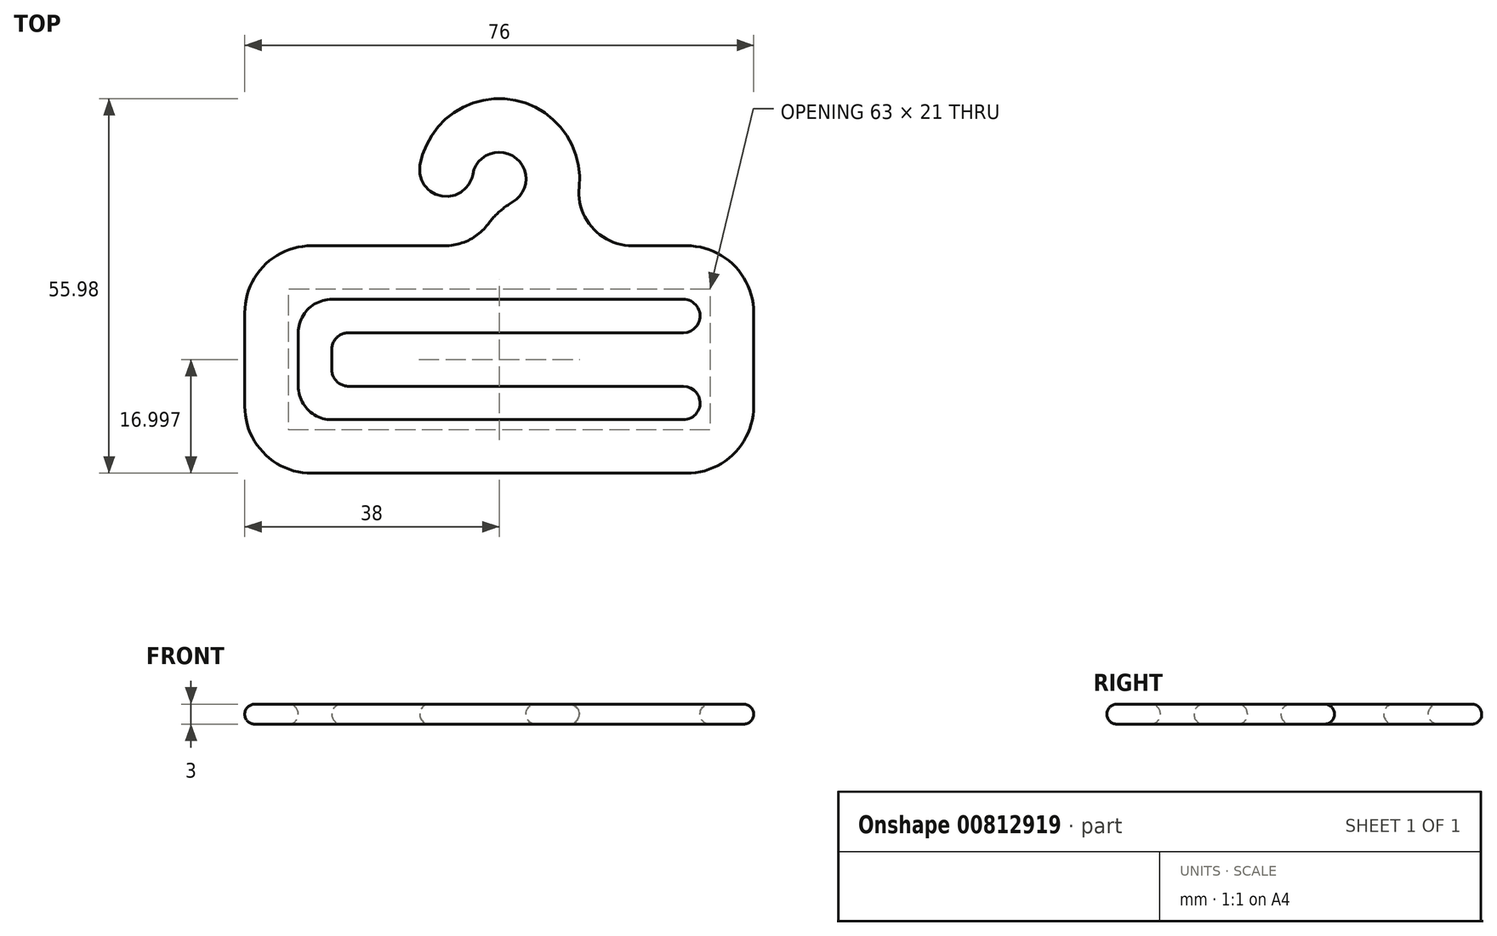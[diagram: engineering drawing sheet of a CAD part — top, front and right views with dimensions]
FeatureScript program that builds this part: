
annotation { "Feature Type Name" : "Feature", "Feature Type Description" : "" }
export const myFeature = defineFeature(function(context is Context, id is Id, definition is map)
    precondition{}
    {
        {
            var Q0;
            Q0=qCreatedBy(makeId("Top.planeOp"),FACE);
            var sketch = newSketch(context, id + "F0", { "sketchPlane" : qUnion([Q0])});
            skPoint(sketch, "E0.visualSharp", {"position": v(0, -8) * mm});
            skArc(sketch, "E0.filletArc", {"start": v(4, -6.93) * mm, "mid": v(2.3, -8.25) * mm, "end": v(1, -9.98) * mm, "construction": true});
            skArc(sketch, "E1", {"start": v(4, -6.93) * mm, "mid": v(4.58, 6.56) * mm, "end": v(-7.88, 1.37) * mm, "construction": true});
            skPoint(sketch, "E2", {"position": v(-7.88, 1.37) * mm});
            skArc(sketch, "E3.1.right", {"start": v(2, -3.46) * mm, "mid": v(0, -4.9) * mm, "end": v(-1.66, -6.73) * mm});
            skArc(sketch, "E3.2.endCap", {"start": v(-3.94, 0.68) * mm, "mid": v(-8.57, -2.57) * mm, "end": v(-11.82, 2.05) * mm});
            skArc(sketch, "E3.2.left", {"start": v(2, -3.46) * mm, "mid": v(2.29, 3.28) * mm, "end": v(-3.94, 0.68) * mm});
            skArc(sketch, "E3.2.right", {"start": v(11.94, -1.19) * mm, "mid": v(1.62, 11.89) * mm, "end": v(-11.82, 2.05) * mm});
            skLineSegment(sketch, "E4.bottom", {"start": v(28, -9.98) * mm, "end": v(19.9, -9.98) * mm});
            skLineSegment(sketch, "E4.top", {"start": v(28, -43.98) * mm, "end": v(-28, -43.98) * mm});
            skLineSegment(sketch, "E4.left", {"start": v(38, -19.98) * mm, "end": v(38, -33.98) * mm});
            skLineSegment(sketch, "E4.right", {"start": v(-38, -19.98) * mm, "end": v(-38, -33.98) * mm});
            skPoint(sketch, "E4.middle", {"position": v(0, -26.98) * mm});
            skLineSegment(sketch, "E5", {"start": v(-30, -22.98) * mm, "end": v(-30, -30.98) * mm});
            skLineSegment(sketch, "E6", {"start": v(-25, -35.98) * mm, "end": v(27.5, -35.98) * mm});
            skLineSegment(sketch, "E7", {"start": v(30, -33.48) * mm, "end": v(30, -33.48) * mm});
            skLineSegment(sketch, "E8", {"start": v(27.5, -30.98) * mm, "end": v(-22.5, -30.98) * mm});
            skLineSegment(sketch, "E9", {"start": v(-25, -28.48) * mm, "end": v(-25, -25.48) * mm});
            skLineSegment(sketch, "E10", {"start": v(-22.5, -22.98) * mm, "end": v(27.5, -22.98) * mm});
            skLineSegment(sketch, "E11", {"start": v(30, -20.48) * mm, "end": v(30, -20.48) * mm});
            skLineSegment(sketch, "E12", {"start": v(27.5, -17.98) * mm, "end": v(-25, -17.98) * mm});
            skPoint(sketch, "E13.visualSharp", {"position": v(-38, -9.98) * mm});
            skArc(sketch, "E13.filletArc", {"start": v(-28, -9.98) * mm, "mid": v(-35.07, -12.91) * mm, "end": v(-38, -19.98) * mm});
            skPoint(sketch, "E14.visualSharp", {"position": v(-30, -17.98) * mm});
            skArc(sketch, "E14.filletArc", {"start": v(-25, -17.98) * mm, "mid": v(-28.54, -19.45) * mm, "end": v(-30, -22.98) * mm});
            skArc(sketch, "E15.filletArc", {"start": v(-22.5, -22.98) * mm, "mid": v(-24.27, -23.71) * mm, "end": v(-25, -25.48) * mm});
            skPoint(sketch, "E16.visualSharp", {"position": v(-38, -43.98) * mm});
            skArc(sketch, "E16.filletArc", {"start": v(-38, -33.98) * mm, "mid": v(-35.07, -41.05) * mm, "end": v(-28, -43.98) * mm});
            skPoint(sketch, "E17.visualSharp", {"position": v(-30, -35.98) * mm});
            skArc(sketch, "E17.filletArc", {"start": v(-30, -30.98) * mm, "mid": v(-28.54, -34.52) * mm, "end": v(-25, -35.98) * mm});
            skArc(sketch, "E18.filletArc", {"start": v(-25, -28.48) * mm, "mid": v(-24.27, -30.25) * mm, "end": v(-22.5, -30.98) * mm});
            skPoint(sketch, "E19.visualSharp", {"position": v(38, -43.98) * mm});
            skArc(sketch, "E19.filletArc", {"start": v(28, -43.98) * mm, "mid": v(35.07, -41.05) * mm, "end": v(38, -33.98) * mm});
            skLineSegment(sketch, "E20", {"start": v(30, -22.98) * mm, "end": v(30, -30.98) * mm, "construction": true});
            skPoint(sketch, "E21.visualSharp", {"position": v(30, -30.98) * mm});
            skArc(sketch, "E21.filletArc", {"start": v(30, -33.48) * mm, "mid": v(29.27, -31.71) * mm, "end": v(27.5, -30.98) * mm});
            skPoint(sketch, "E22.visualSharp", {"position": v(30, -35.98) * mm});
            skArc(sketch, "E22.filletArc", {"start": v(27.5, -35.98) * mm, "mid": v(29.27, -35.25) * mm, "end": v(30, -33.48) * mm});
            skPoint(sketch, "E23.visualSharp", {"position": v(30, -17.98) * mm});
            skArc(sketch, "E23.filletArc", {"start": v(30, -20.48) * mm, "mid": v(29.27, -18.71) * mm, "end": v(27.5, -17.98) * mm});
            skPoint(sketch, "E24.visualSharp", {"position": v(30, -22.98) * mm});
            skArc(sketch, "E24.filletArc", {"start": v(27.5, -22.98) * mm, "mid": v(29.27, -22.25) * mm, "end": v(30, -20.48) * mm});
            skPoint(sketch, "E25.visualSharp", {"position": v(38, -9.98) * mm});
            skArc(sketch, "E25.filletArc", {"start": v(38, -19.98) * mm, "mid": v(35.07, -12.91) * mm, "end": v(28, -9.98) * mm});
            skArc(sketch, "E26", {"start": v(1, -9.98) * mm, "mid": v(0.25, -11.86) * mm, "end": v(0, -13.86) * mm, "construction": true});
            skLineSegment(sketch, "E27.trimOffspring", {"start": v(-8.1, -9.98) * mm, "end": v(-28, -9.98) * mm});
            skPoint(sketch, "E28.visualSharp", {"position": v(-3.36, -9.98) * mm});
            skArc(sketch, "E28.filletArc", {"start": v(-8.1, -9.98) * mm, "mid": v(-4.49, -9.12) * mm, "end": v(-1.66, -6.73) * mm});
            skPoint(sketch, "E29.visualSharp", {"position": v(6.66, -9.98) * mm});
            skArc(sketch, "E29.filletArc", {"start": v(11.94, -1.19) * mm, "mid": v(13.97, -7.35) * mm, "end": v(19.9, -9.98) * mm});
            skSolve(sketch);
        }
        {
            var Q0;
            Q0 = qSketchRegion(id + "F0", true);
            extrude(context, id + "F1", {"entities" : qUnion([Q0]), "depth" : 3 * mm, "offsetDistance" : 25 * mm});
        }
        {
            var Q0;
            Q0=makeQuery(id+"F0.imprint","IMPRINT",FACE,{"disambiguationData":[TD([[makeQuery(id+"F0.imprint","IMPRINT",EDGE,{"derivedFrom":sQuery(id+"F0.wireOp",EDGE,"E5")}),1.0]])]});
            extrude(context, id + "F2", {"entities" : qUnion([Q0]), "operationType" : NewBodyOperationType.REMOVE, "oppositeDirection" : true, "depth" : 3 * mm, "offsetDistance" : 25 * mm});
        }
        {
            var Q0;
            Q0=makeQuery(id+"F1.opExtrude","CAP_EDGE",EDGE,{"disambiguationData":[OSD([sQuery(id+"F0.wireOp",EDGE,"E8")])],"isStart":false});
            var Q1;
            Q1=makeQuery(id+"F1.opExtrude","CAP_EDGE",EDGE,{"disambiguationData":[OSD([sQuery(id+"F0.wireOp",EDGE,"E29.filletArc")])],"isStart":false});
            var Q2;
            Q2=makeQuery(id+"F1.opExtrude","CAP_EDGE",EDGE,{"disambiguationData":[OSD([sQuery(id+"F0.wireOp",EDGE,"E12")])],"isStart":true});
            var Q3;
            Q3=makeQuery(id+"F1.opExtrude","CAP_EDGE",EDGE,{"disambiguationData":[OSD([sQuery(id+"F0.wireOp",EDGE,"E3.2.endCap")])],"isStart":true});
            fillet(context, id + "F3", {"entities" : qUnion([Q0, Q1, Q2, Q3]), "radius" : 1.5 * mm, "tangentPropagation" : true, "allowEdgeOverflow" : false});
        }
    });
